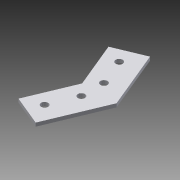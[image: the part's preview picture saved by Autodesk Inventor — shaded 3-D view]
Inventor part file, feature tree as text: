
AUTODESK INVENTOR PART (.ipt)
format: ipt  version: 2015 SP1 (Build 190203100, 203)  size: 97,280 bytes
history: native  units: in
note: dims shown in document units (in); Inventor stores cm internally (conversion verified against a paired STEP export)
features: extrude x1, sketch x1
ambient origin geometry x8: Origin, YZ Plane, XZ Plane, XY Plane, X Axis, Y Axis, Z Axis, Center Point
bodies: Solid1 (feature_tree)
feature tree (2):
  extrude  "Extrusion1"  TaperAngle=135.0deg  [1 undecoded]
  sketch  "Sketch1"  dims[d1=2.2in d2=135.0deg d3=0.1464in d7=0.25in d15=0.125in d16=0.0in d17=1.13in d19=1.5748in d21=1.0in d22=0.3937in d24=1.0in d26=4.0in d27=0.5in d29=0.5in d30=0.473in]
note: 1 required parameter value undecoded (feature->parameter linkage not recoverable at this tier; creation-order binding heuristic only, values carry confidence <= 0.55)
